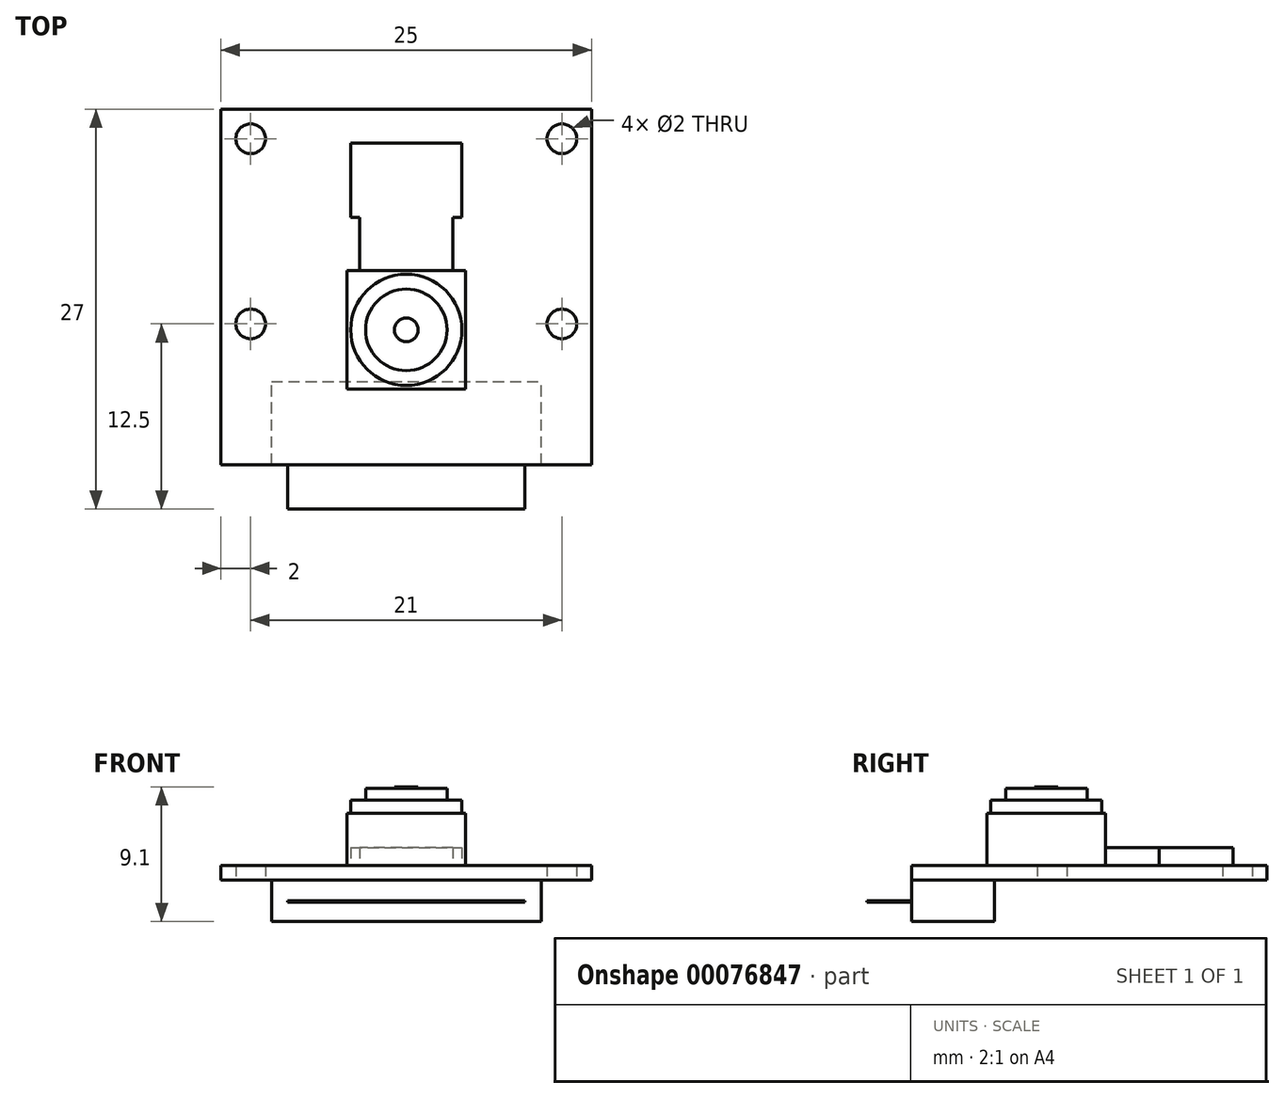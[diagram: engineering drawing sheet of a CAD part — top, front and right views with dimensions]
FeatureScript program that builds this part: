
annotation { "Feature Type Name" : "Feature", "Feature Type Description" : "" }
export const myFeature = defineFeature(function(context is Context, id is Id, definition is map)
    precondition{}
    {
        {
            var Q0;
            Q0=qCreatedBy(makeId("Top.planeOp"),FACE);
            var sketch = newSketch(context, id + "F0", { "sketchPlane" : qUnion([Q0])});
            skLineSegment(sketch, "E0.rect.bottom", {"start": v(12.5, 12) * mm, "end": v(-12.5, 12) * mm});
            skLineSegment(sketch, "E0.rect.top", {"start": v(12.5, -12) * mm, "end": v(-12.5, -12) * mm});
            skLineSegment(sketch, "E0.rect.left", {"start": v(12.5, 12) * mm, "end": v(12.5, -12) * mm});
            skLineSegment(sketch, "E0.rect.right", {"start": v(-12.5, 12) * mm, "end": v(-12.5, -12) * mm});
            skPoint(sketch, "E0.rect.middle", {"position": v(0, 0) * mm});
            skCircle(sketch, "E1", {"center": v(-10.5, 10) * mm, "radius": 1 * mm});
            skCircle(sketch, "E2", {"center": v(-10.5, -2.5) * mm, "radius": 1 * mm});
            skLineSegment(sketch, "E3", {"start": v(-10.5, 10) * mm, "end": v(-10.5, -12) * mm, "construction": true});
            skCircle(sketch, "E4.MirrorC", {"center": v(10.5, 10) * mm, "radius": 1 * mm});
            skCircle(sketch, "E5.MirrorC", {"center": v(10.5, -2.5) * mm, "radius": 1 * mm});
            skSolve(sketch);
        }
        {
            var Q0;
            Q0=makeQuery(id+"F0.imprint","IMPRINT",FACE,{"disambiguationData":[TD([[makeQuery(id+"F0.imprint","IMPRINT",EDGE,{"derivedFrom":sQuery(id+"F0.wireOp",EDGE,"E0.rect.bottom")}),1.0]])]});
            extrude(context, id + "F1", {"entities" : qUnion([Q0]), "depth" : 1 * mm});
        }
        {
            var Q0;
            Q0=makeQuery(id+"F1.opExtrude","CAP_FACE",FACE,{"disambiguationData":[OSD([sQuery(id+"F0.wireOp",EDGE,"E0.rect.bottom"),sQuery(id+"F0.wireOp",EDGE,"E0.rect.top"),sQuery(id+"F0.wireOp",EDGE,"E0.rect.left"),sQuery(id+"F0.wireOp",EDGE,"E0.rect.right"),sQuery(id+"F0.wireOp",EDGE,"E1"),sQuery(id+"F0.wireOp",EDGE,"E2"),sQuery(id+"F0.wireOp",EDGE,"E4.MirrorC"),sQuery(id+"F0.wireOp",EDGE,"E5.MirrorC")])],"isStart":false});
            var sketch = newSketch(context, id + "F2", { "sketchPlane" : qUnion([Q0])});
            skLineSegment(sketch, "E6", {"start": v(-12.5, -2.9) * mm, "end": v(12.5, -2.9) * mm, "construction": true});
            skLineSegment(sketch, "E7.rect.bottom", {"start": v(4, 1.1) * mm, "end": v(-4, 1.1) * mm});
            skLineSegment(sketch, "E7.rect.top", {"start": v(4, -6.9) * mm, "end": v(-4, -6.9) * mm});
            skLineSegment(sketch, "E7.rect.left", {"start": v(4, 1.1) * mm, "end": v(4, -6.9) * mm});
            skLineSegment(sketch, "E7.rect.right", {"start": v(-4, 1.1) * mm, "end": v(-4, -6.9) * mm});
            skPoint(sketch, "E7.rect.middle", {"position": v(0, -2.9) * mm});
            skCircle(sketch, "E8", {"center": v(0, -2.9) * mm, "radius": 3.75 * mm});
            skCircle(sketch, "E9", {"center": v(0, -2.9) * mm, "radius": 2.75 * mm});
            skLineSegment(sketch, "E10.bottom", {"start": v(-3.4, 1.1) * mm, "end": v(3.4, 1.1) * mm});
            skSolve(sketch);
        }
        {
            var Q0;
            Q0=qSketchRegion(id+"F2",true);
            var Q1;
            Q1=makeQuery(id+"F2.imprint","IMPRINT",FACE,{"disambiguationData":[TD([[makeQuery(id+"F2.imprint","IMPRINT",EDGE,{"derivedFrom":sQuery(id+"F2.wireOp",EDGE,"E8")}),1.0]])]});
            var Q2;
            Q2=makeQuery(id+"F2.imprint","IMPRINT",FACE,{"disambiguationData":[TD([[makeQuery(id+"F2.imprint","IMPRINT",EDGE,{"derivedFrom":sQuery(id+"F2.wireOp",EDGE,"E9")}),1.0]])]});
            extrude(context, id + "F3", {"entities" : qUnion([Q0, Q1, Q2]), "depth" : 3.5 * mm});
        }
        {
            var Q0;
            Q0=makeQuery(id+"F2.imprint","IMPRINT",FACE,{"disambiguationData":[TD([[makeQuery(id+"F2.imprint","IMPRINT",EDGE,{"derivedFrom":sQuery(id+"F2.wireOp",EDGE,"E8")}),1.0]])]});
            var Q1;
            Q1=makeQuery(id+"F2.imprint","IMPRINT",FACE,{"disambiguationData":[TD([[makeQuery(id+"F2.imprint","IMPRINT",EDGE,{"derivedFrom":sQuery(id+"F2.wireOp",EDGE,"E9")}),1.0]])]});
            extrude(context, id + "F4", {"entities" : qUnion([Q0, Q1]), "operationType" : NewBodyOperationType.ADD, "depth" : (3.5 + 0.9) * mm});
        }
        {
            var Q0;
            Q0=makeQuery(id+"F2.imprint","IMPRINT",FACE,{"disambiguationData":[TD([[makeQuery(id+"F2.imprint","IMPRINT",EDGE,{"derivedFrom":sQuery(id+"F2.wireOp",EDGE,"E9")}),1.0]])]});
            extrude(context, id + "F5", {"entities" : qUnion([Q0]), "operationType" : NewBodyOperationType.ADD, "depth" : 5.2 * mm});
        }
        {
            var Q0;
            Q0=makeQuery(id+"F5.opExtrude","CAP_FACE",FACE,{"disambiguationData":[OSD([sQuery(id+"F2.wireOp",EDGE,"E9")])],"isStart":false});
            var sketch = newSketch(context, id + "F6", { "sketchPlane" : qUnion([Q0])});
            skCircle(sketch, "E11", {"center": v(0, -2.9) * mm, "radius": 0.8 * mm});
            skSolve(sketch);
        }
        {
            var Q0;
            Q0=makeQuery(id+"F6.imprint","IMPRINT",FACE,{"disambiguationData":[TD([[makeQuery(id+"F6.imprint","IMPRINT",EDGE,{"derivedFrom":sQuery(id+"F6.wireOp",EDGE,"E11")}),1.0]])]});
            extrude(context, id + "F7", {"entities" : qUnion([Q0]), "depth" : 0.1 * mm});
        }
        {
            var Q0;
            Q0=makeQuery(id+"F1.opExtrude","CAP_FACE",FACE,{"disambiguationData":[OSD([sQuery(id+"F0.wireOp",EDGE,"E0.rect.bottom"),sQuery(id+"F0.wireOp",EDGE,"E0.rect.top"),sQuery(id+"F0.wireOp",EDGE,"E0.rect.left"),sQuery(id+"F0.wireOp",EDGE,"E0.rect.right"),sQuery(id+"F0.wireOp",EDGE,"E1"),sQuery(id+"F0.wireOp",EDGE,"E2"),sQuery(id+"F0.wireOp",EDGE,"E4.MirrorC"),sQuery(id+"F0.wireOp",EDGE,"E5.MirrorC")])],"isStart":true});
            var sketch = newSketch(context, id + "F8", { "sketchPlane" : qUnion([Q0])});
            skLineSegment(sketch, "E12.bottom", {"start": v(-9.1, 12) * mm, "end": v(9.1, 12) * mm});
            skLineSegment(sketch, "E12.top", {"start": v(-9.1, 6.4) * mm, "end": v(9.1, 6.4) * mm});
            skLineSegment(sketch, "E12.left", {"start": v(-9.1, 12) * mm, "end": v(-9.1, 6.4) * mm});
            skLineSegment(sketch, "E12.right", {"start": v(9.1, 12) * mm, "end": v(9.1, 6.4) * mm});
            skSolve(sketch);
        }
        {
            var Q0;
            Q0=qSketchRegion(id+"F8",true);
            extrude(context, id + "F9", {"entities" : qUnion([Q0]), "depth" : 2.8 * mm});
        }
        {
            var Q0;
            Q0=makeQuery(id+"F2.imprint","IMPRINT",FACE,{"disambiguationData":[TD([[makeQuery(id+"F2.imprint","IMPRINT",EDGE,{"derivedFrom":sQuery(id+"F2.wireOp",EDGE,"E7.rect.top")}),1.0]])]});
            var sketch = newSketch(context, id + "F10", { "sketchPlane" : qUnion([Q0])});
            skLineSegment(sketch, "E13.bottom", {"start": v(-3.75, 1.1) * mm, "end": v(3.75, 1.1) * mm});
            skLineSegment(sketch, "E13.top", {"start": v(-3.75, 9.7) * mm, "end": v(3.75, 9.7) * mm});
            skLineSegment(sketch, "E13.left", {"start": v(-3.75, 4.7) * mm, "end": v(-3.75, 9.7) * mm});
            skLineSegment(sketch, "E13.right", {"start": v(3.75, 4.7) * mm, "end": v(3.75, 9.7) * mm});
            skLineSegment(sketch, "E14", {"start": v(-3.75, 4.7) * mm, "end": v(-3.15, 4.7) * mm});
            skLineSegment(sketch, "E15", {"start": v(-3.15, 4.7) * mm, "end": v(-3.15, 1.1) * mm});
            skLineSegment(sketch, "E16", {"start": v(3.15, 4.7) * mm, "end": v(3.15, 1.1) * mm});
            skLineSegment(sketch, "E17.trimOffspring", {"start": v(3.15, 4.7) * mm, "end": v(3.75, 4.7) * mm});
            skSolve(sketch);
        }
        {
            var Q0;
            Q0=qSketchRegion(id+"F10",true);
            extrude(context, id + "F11", {"entities" : qUnion([Q0]), "depth" : 1.2 * mm});
        }
        {
            var Q0;
            Q0=makeQuery(id+"F1.opExtrude","CAP_FACE",FACE,{"disambiguationData":[OSD([sQuery(id+"F0.wireOp",EDGE,"E0.rect.bottom"),sQuery(id+"F0.wireOp",EDGE,"E0.rect.top"),sQuery(id+"F0.wireOp",EDGE,"E0.rect.left"),sQuery(id+"F0.wireOp",EDGE,"E0.rect.right"),sQuery(id+"F0.wireOp",EDGE,"E1"),sQuery(id+"F0.wireOp",EDGE,"E2"),sQuery(id+"F0.wireOp",EDGE,"E4.MirrorC"),sQuery(id+"F0.wireOp",EDGE,"E5.MirrorC")])],"isStart":true});
            cPlane(context, id + "F12", {"entities" : qUnion([Q0]), "cplaneType" : CPlaneType.OFFSET, "offset" : (2.8 / 2) * mm, "width" : 150 * mm, "height" : 150 * mm});
        }
        {
            var Q0;
            Q0=qCreatedBy(id+"F12.planeOp",FACE);
            var sketch = newSketch(context, id + "F13", { "sketchPlane" : qUnion([Q0])});
            skLineSegment(sketch, "E18.bottom", {"start": v(-8, 12) * mm, "end": v(8, 12) * mm});
            skLineSegment(sketch, "E18.top", {"start": v(-8, 15) * mm, "end": v(8, 15) * mm});
            skLineSegment(sketch, "E18.left", {"start": v(-8, 12) * mm, "end": v(-8, 15) * mm});
            skLineSegment(sketch, "E18.right", {"start": v(8, 12) * mm, "end": v(8, 15) * mm});
            skSolve(sketch);
        }
        {
            var Q0;
            Q0=makeQuery(id+"F13.imprint","IMPRINT",FACE,{"disambiguationData":[TD([[makeQuery(id+"F13.imprint","IMPRINT",EDGE,{"derivedFrom":sQuery(id+"F13.wireOp",EDGE,"E18.bottom")}),1.0]])]});
            extrude(context, id + "F14", {"entities" : qUnion([Q0]), "depth" : 0.1 * mm});
        }
    });
